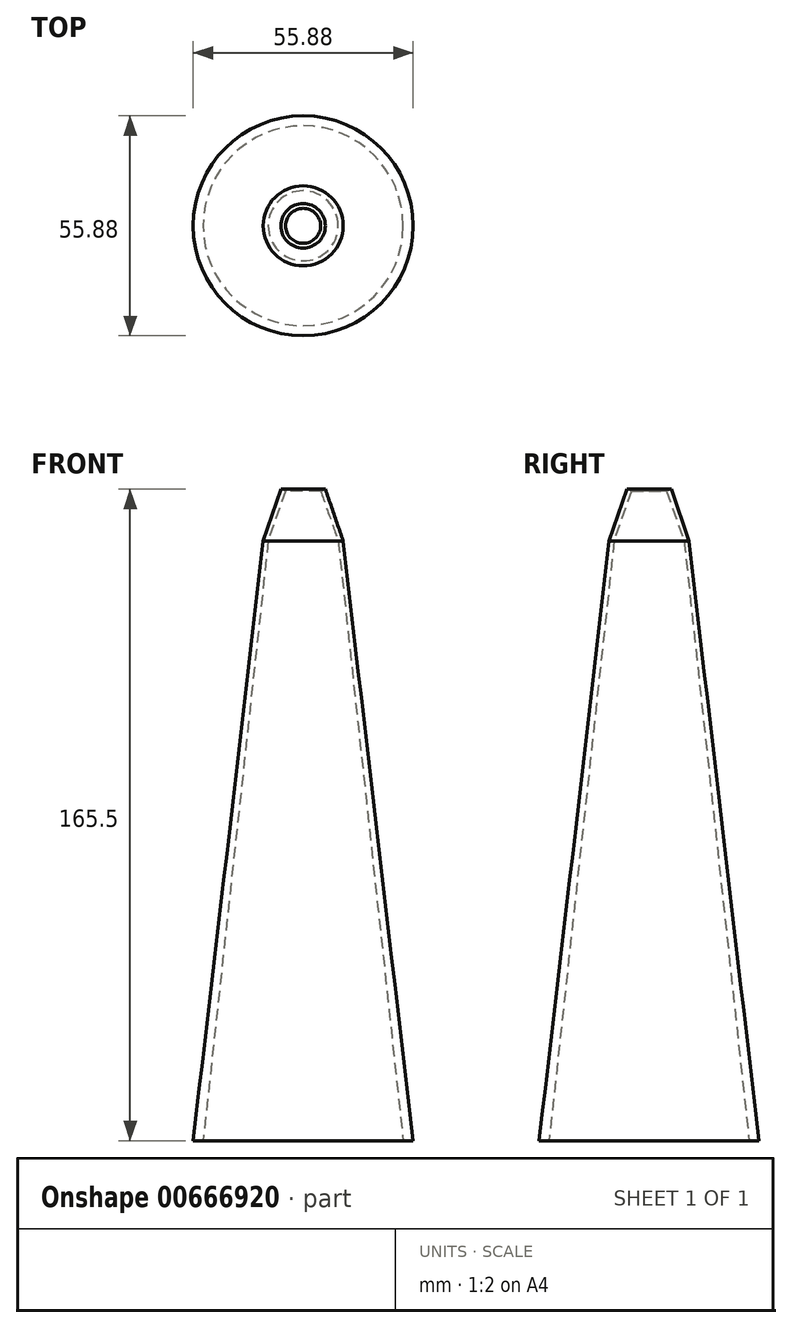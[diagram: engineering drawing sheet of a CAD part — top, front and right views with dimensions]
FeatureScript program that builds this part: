
annotation { "Feature Type Name" : "Feature", "Feature Type Description" : "" }
export const myFeature = defineFeature(function(context is Context, id is Id, definition is map)
    precondition{}
    {
        {
            var Q0;
            Q0=qCreatedBy(makeId("Front.planeOp"),FACE);
            var sketch = newSketch(context, id + "F0", { "sketchPlane" : qUnion([Q0])});
            skLineSegment(sketch, "E0", {"start": v(0, 93.8) * mm, "end": v(0, -71.3) * mm, "construction": true});
            skLineSegment(sketch, "E1", {"start": v(-25.36, -71.3) * mm, "end": v(-25.4, -71.3) * mm});
            skLineSegment(sketch, "E2", {"start": v(-8.9, 81.1) * mm, "end": v(-25.4, -71.3) * mm});
            skLineSegment(sketch, "E3", {"start": v(8.9, 81.1) * mm, "end": v(25.4, -71.3) * mm});
            skLineSegment(sketch, "E4", {"start": v(4.44, 93.8) * mm, "end": v(8.89, 81.1) * mm});
            skLineSegment(sketch, "E5", {"start": v(-4.44, 93.78) * mm, "end": v(-8.9, 81.1) * mm});
            skLineSegment(sketch, "E6", {"start": v(-25.4, -71.3) * mm, "end": v(-27.94, -71.3) * mm});
            skLineSegment(sketch, "E7", {"start": v(25.4, -71.3) * mm, "end": v(27.94, -71.3) * mm});
            skLineSegment(sketch, "E8", {"start": v(-4.44, 93.78) * mm, "end": v(-5.64, 94.2) * mm});
            skLineSegment(sketch, "E9", {"start": v(4.44, 93.8) * mm, "end": v(5.64, 94.21) * mm});
            skLineSegment(sketch, "E10", {"start": v(5.64, 94.21) * mm, "end": v(10.39, 80.94) * mm});
            skLineSegment(sketch, "E11", {"start": v(-5.64, 94.2) * mm, "end": v(-10.16, 81.1) * mm});
            skArc(sketch, "E12", {"start": v(-27.94, -71.3) * mm, "mid": v(-19, 4.9) * mm, "end": v(-10.16, 81.1) * mm});
            skArc(sketch, "E13", {"start": v(10.39, 80.94) * mm, "mid": v(19.03, 4.8) * mm, "end": v(27.94, -71.3) * mm});
            skSolve(sketch);
        }
        {
            var Q0;
            Q0=makeQuery(id+"F0.imprint","IMPRINT",FACE,{"disambiguationData":[TD([[makeQuery(id+"F0.imprint","IMPRINT",EDGE,{"derivedFrom":sQuery(id+"F0.wireOp",EDGE,"E2")}),-1.0]])]});
            var Q1;
            Q1=sQuery(id+"F0.wireOp",EDGE,"E0");
            revolve(context, id + "F1", {"entities" : qUnion([Q0]), "axis" : qUnion([Q1]), "revolveType" : RevolveType.FULL});
        }
    });
